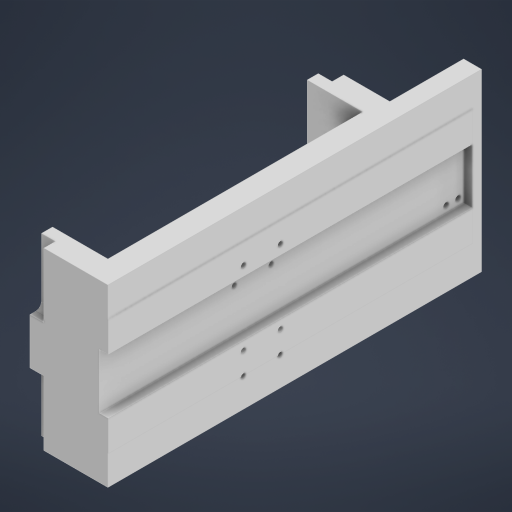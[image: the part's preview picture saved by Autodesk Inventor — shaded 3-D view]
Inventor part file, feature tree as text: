
AUTODESK INVENTOR PART (.ipt)
format: ipt  version: 2024 (Build 280153000, 153)  size: 358,912 bytes
history: native  units: mm
features: extrude x10, sketch x10, projected_geometry x5, other x1, fillet x1
ambient origin geometry x8: Origin, YZ Plane, XZ Plane, XY Plane, X Axis, Y Axis, Z Axis, Center Point
bodies: Body1 (feature_tree)
feature tree (27):
  other  "Твердое тело1"
  extrude  "Выдавливание1"  Depth=60.0mm
  extrude  "Выдавливание2"  Depth=25.0mm
  extrude  "Выдавливание3"  Depth=25.0mm
  extrude  "Выдавливание4"  Depth=190.0mm TaperAngle=0.0deg
  extrude  "Выдавливание5"  Depth=32.0mm
  fillet  "Сопряжение1"  Radius=32.0mm
  extrude  "Выдавливание6"  Depth=0.5mm TaperAngle=0.0deg
  extrude  "Выдавливание7"  Depth=20.0mm
  extrude  "Выдавливание8"  Depth=70.0mm TaperAngle=0.0deg
  extrude  "Extrusion9"  Depth=33.0mm
  extrude  "Extrusion10"  Depth=33.0mm
  sketch  "Эскиз1"
  sketch  "Эскиз2"
  projected_geometry  "Спроецированная петля1"
  sketch  "Эскиз4"
  projected_geometry  "Спроецированная петля3"
  sketch  "Эскиз5"
  projected_geometry  "Спроецированная петля4"
  sketch  "Эскиз6"
  projected_geometry  "Спроецированная петля5"
  projected_geometry  "Спроецированная петля6"
  sketch  "Эскиз8"
  sketch  "Эскиз9"
  sketch  "Эскиз10"
  sketch  "Sketch11"  dims[d0=300.0mm d1=60.0mm]
  sketch  "Sketch12"  dims[d2=25.0mm d3=25.0mm d5=25.0mm d6=190.0mm d7=0.0mm d8=32.0mm d9=32.0mm d10=0.5mm d11=0.0mm d12=20.0mm d13=70.0mm d14=0.0mm d15=33.0mm d16=33.0mm d17=10.0mm d18=0.0mm d19=15.0mm d20=0.0mm d21=70.0mm d22=70.0mm d23=6.0mm d24=6.0mm d25=46.0mm d26=13.0mm d27=100.0mm d28=0.0mm d29=10.0mm d30=0.0mm d31=33.0mm d32=0.0mm d33=25.0mm d34=24.5mm d35=24.5mm d36=0.5mm d37=0.5mm d38=200.0mm d39=0.0mm d40=80.0mm d41=80.0mm d42=80.0mm d43=80.0mm d44=40.0mm d45=0.0mm d46=15.0mm d47=15.0mm]
